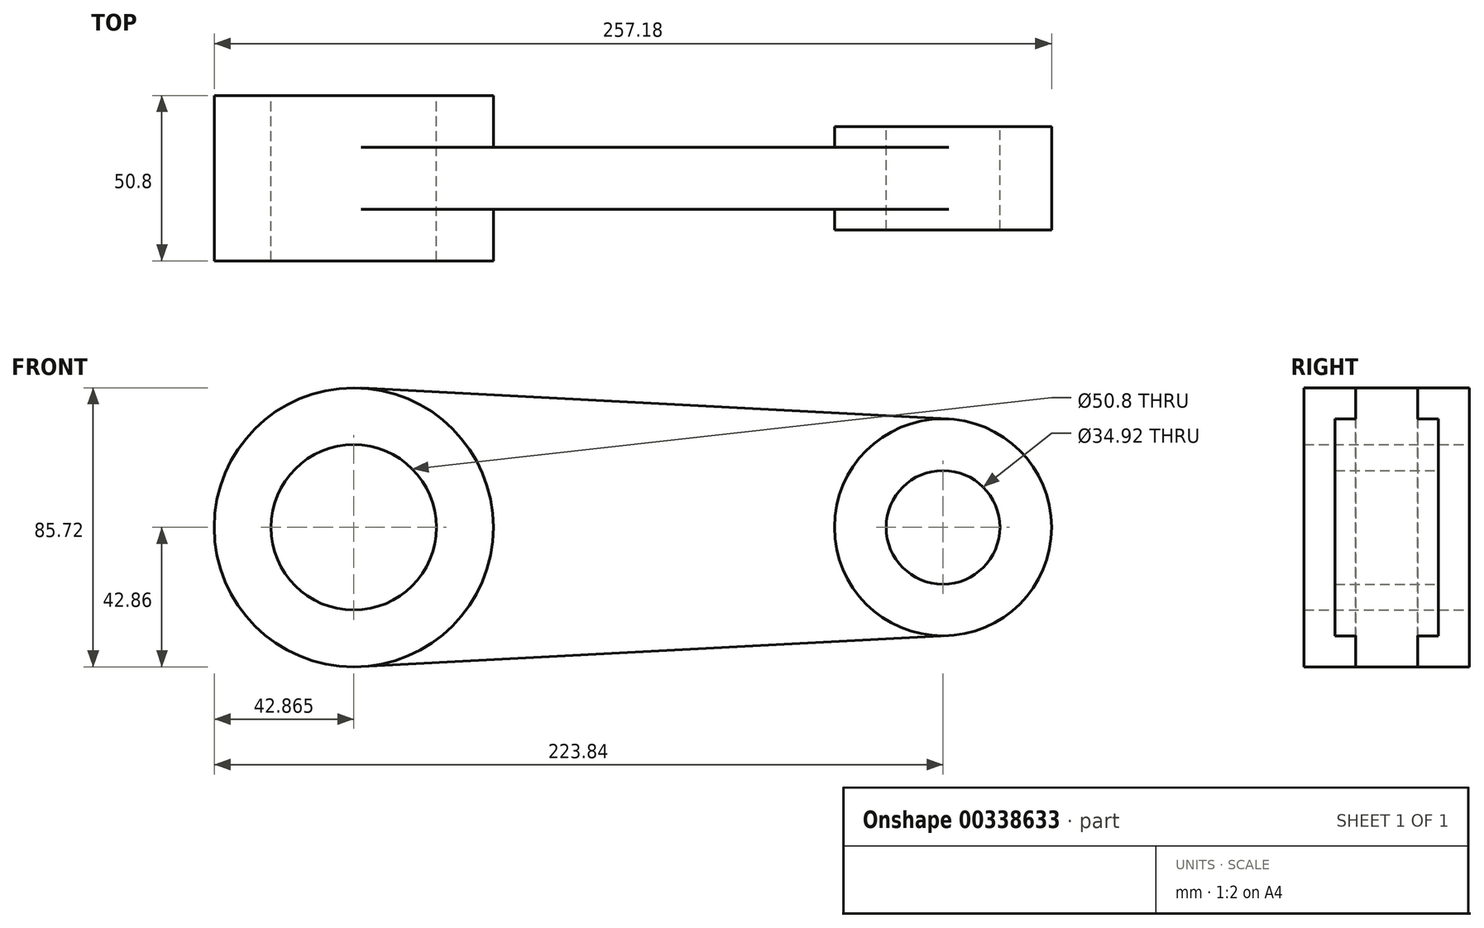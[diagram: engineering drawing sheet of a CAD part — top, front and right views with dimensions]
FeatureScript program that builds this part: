
annotation { "Feature Type Name" : "Feature", "Feature Type Description" : "" }
export const myFeature = defineFeature(function(context is Context, id is Id, definition is map)
    precondition{}
    {
        {
            var Q0;
            Q0=qCreatedBy(makeId("Front.planeOp"),FACE);
            var sketch = newSketch(context, id + "F0", { "sketchPlane" : qUnion([Q0])});
            skCircle(sketch, "E0", {"center": v(155.23, 0) * mm, "radius": 17.46 * mm});
            skCircle(sketch, "E1", {"center": v(-25.74, 0) * mm, "radius": 25.4 * mm});
            skCircle(sketch, "E2", {"center": v(-25.74, 0) * mm, "radius": 42.86 * mm});
            skCircle(sketch, "E3", {"center": v(155.23, 0) * mm, "radius": 33.34 * mm});
            skLineSegment(sketch, "E4", {"start": v(-23.49, -42.8) * mm, "end": v(156.98, -33.3) * mm});
            skLineSegment(sketch, "E5", {"start": v(-23.49, 42.8) * mm, "end": v(156.98, 33.3) * mm});
            skSolve(sketch);
        }
        {
            var Q0;
            {var subQ0=sQuery(id+"F0.wireOp",EDGE,"E5");var subQ1=sQuery(id+"F0.wireOp",EDGE,"E2");var subQ2=makeQuery(id+"F0.imprint","INTERSECT",VERTEX,{"disambiguationData":[OD(1.0)],"derivedFrom":[subQ1,subQ0]});Q0=makeQuery(id+"F0.imprint","IMPRINT",FACE,{"disambiguationData":[TD([[makeQuery(id+"F0.imprint","IMPRINT",EDGE,{"disambiguationData":[TD([[subQ2,1.0]])],"derivedFrom":subQ1}),-1.0]])]});}
            extrude(context, id + "F1", {"entities" : qUnion([Q0]), "depth" : 19.05 * mm, "symmetric" : true});
        }
        {
            var Q0;
            Q0=makeQuery(id+"F0.imprint","IMPRINT",FACE,{"disambiguationData":[TD([[makeQuery(id+"F0.imprint","IMPRINT",EDGE,{"derivedFrom":sQuery(id+"F0.wireOp",EDGE,"E1")}),-1.0]])]});
            extrude(context, id + "F2", {"entities" : qUnion([Q0]), "operationType" : NewBodyOperationType.ADD, "depth" : 50.8 * mm, "symmetric" : true});
        }
        {
            var Q0;
            Q0=makeQuery(id+"F0.imprint","IMPRINT",FACE,{"disambiguationData":[TD([[makeQuery(id+"F0.imprint","IMPRINT",EDGE,{"derivedFrom":sQuery(id+"F0.wireOp",EDGE,"E0")}),-1.0]])]});
            extrude(context, id + "F3", {"entities" : qUnion([Q0]), "operationType" : NewBodyOperationType.ADD, "depth" : 31.75 * mm, "symmetric" : true});
        }
    });
